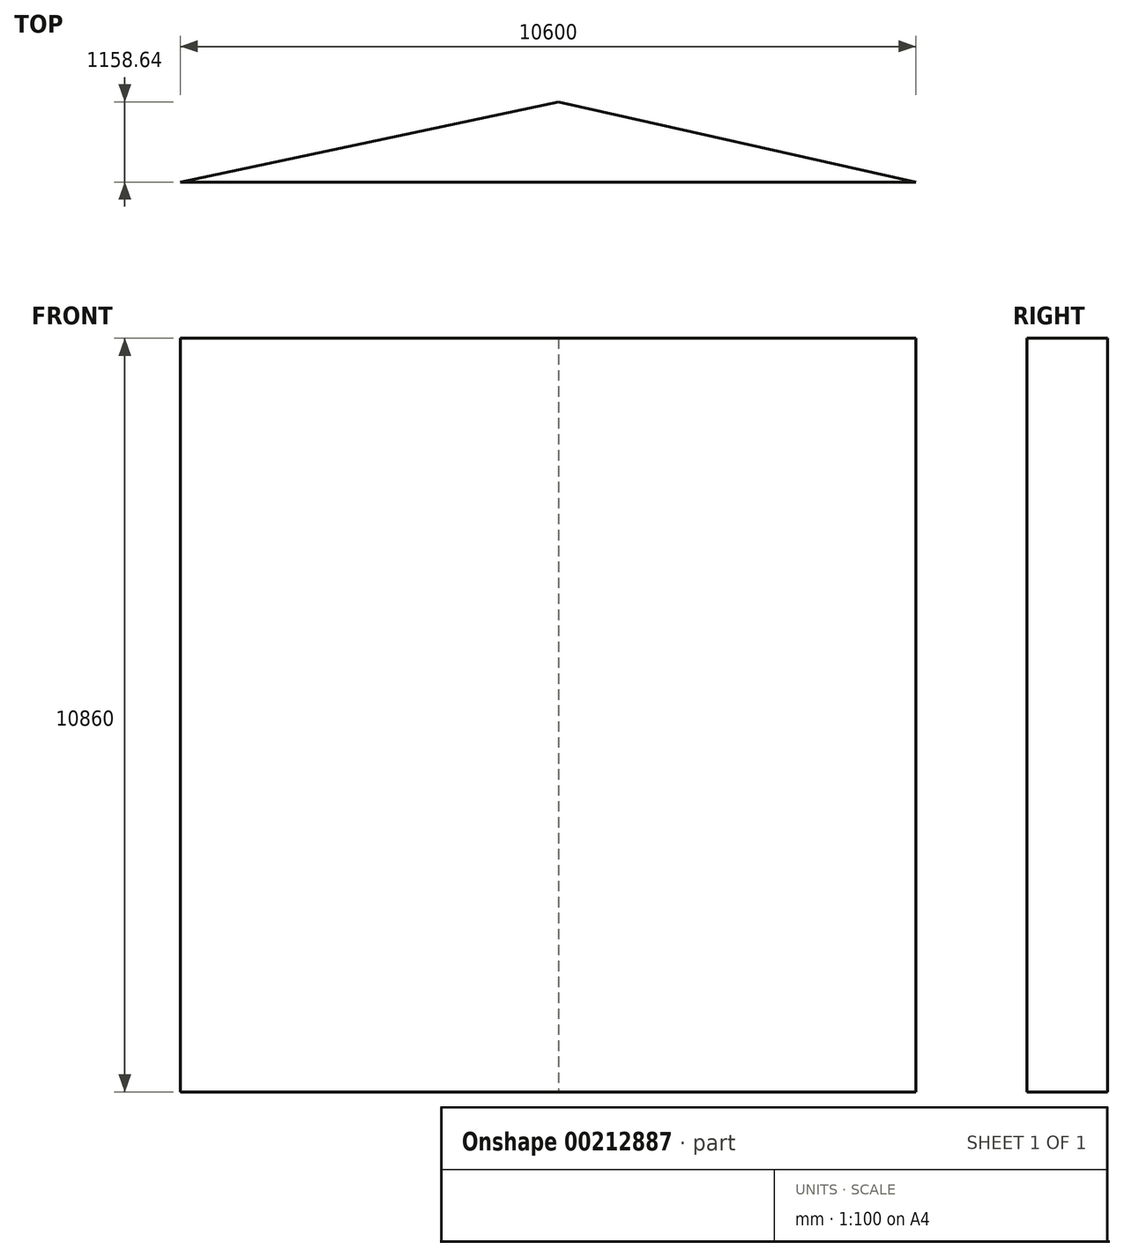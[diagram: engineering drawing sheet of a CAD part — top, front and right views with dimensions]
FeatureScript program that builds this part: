
annotation { "Feature Type Name" : "Feature", "Feature Type Description" : "" }
export const myFeature = defineFeature(function(context is Context, id is Id, definition is map)
    precondition{}
    {
        {
            var Q0;
            Q0=qCreatedBy(makeId("Top.planeOp"),FACE);
            var sketch = newSketch(context, id + "F0", { "sketchPlane" : qUnion([Q0])});
            skLineSegment(sketch, "E0.top", {"start": v(-5450.97, -5962.07) * mm, "end": v(5149.03, -5962.07) * mm});
            skPoint(sketch, "E0.middle", {"position": v(0, 0) * mm});
            skLineSegment(sketch, "E1", {"start": v(-5450.97, -5962.07) * mm, "end": v(0, -4803.43) * mm});
            skLineSegment(sketch, "E2", {"start": v(0, -4803.43) * mm, "end": v(5149.03, -5962.07) * mm});
            skPoint(sketch, "E0.left.start.orphan", {"position": v(-5149.03, 5962.07) * mm});
            skPoint(sketch, "E0.right.start.orphan", {"position": v(5450.97, 5962.07) * mm});
            skSolve(sketch);
        }
        {
            var Q0;
            Q0=qSketchRegion(id+"F0",true);
            extrude(context, id + "F1", {"entities" : qUnion([Q0]), "depth" : (8500 + 360 + 2000) * mm});
        }
    });
